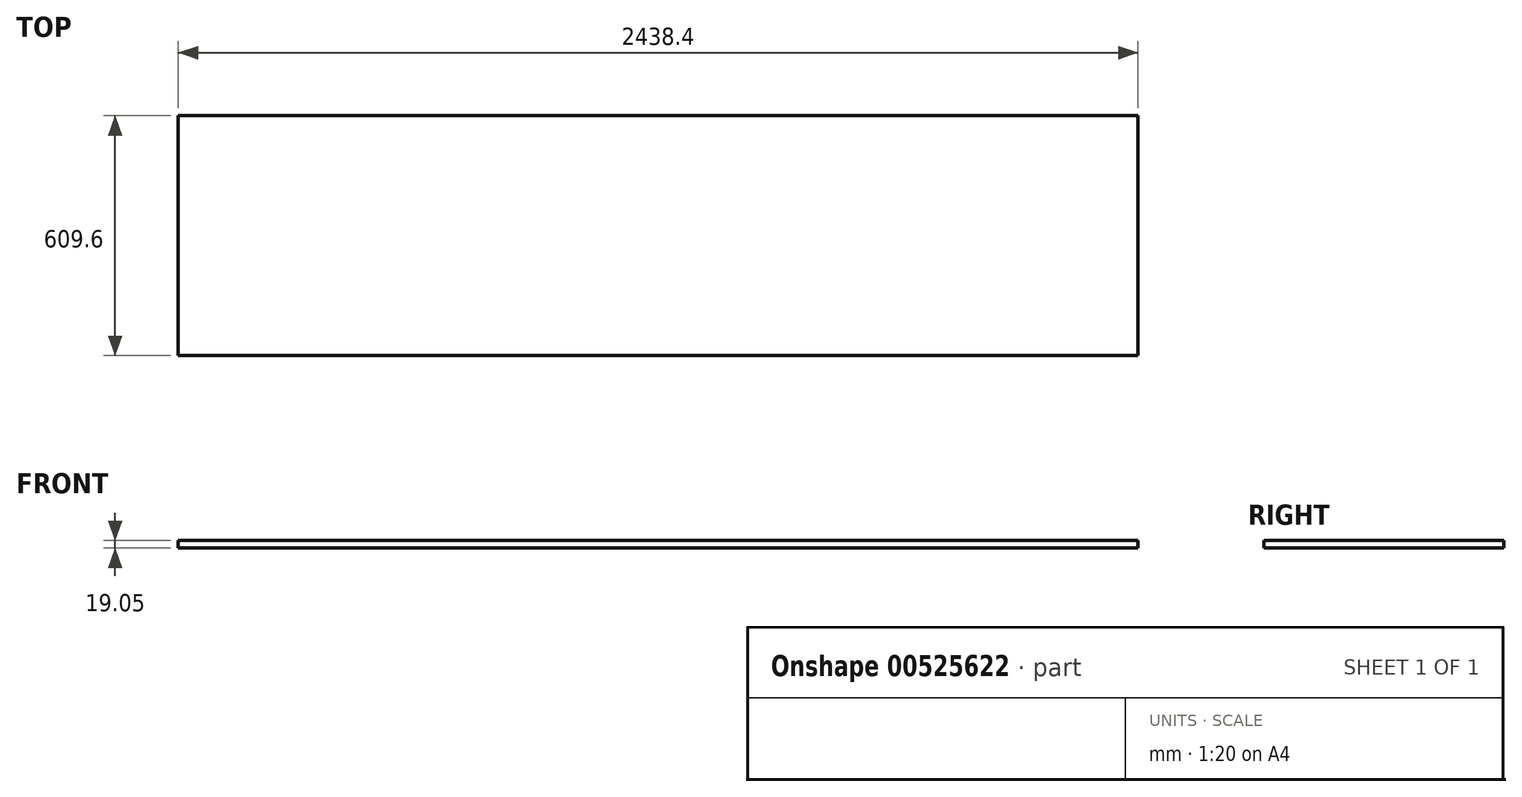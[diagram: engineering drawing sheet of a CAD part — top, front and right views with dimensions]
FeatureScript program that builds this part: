
annotation { "Feature Type Name" : "Feature", "Feature Type Description" : "" }
export const myFeature = defineFeature(function(context is Context, id is Id, definition is map)
    precondition{}
    {
        {
            var Q0;
            Q0=qCreatedBy(makeId("Top.planeOp"),FACE);
            var sketch = newSketch(context, id + "F0", { "sketchPlane" : qUnion([Q0])});
            skLineSegment(sketch, "E0.bottom", {"start": v(1219.2, -304.8) * mm, "end": v(-1219.2, -304.8) * mm});
            skLineSegment(sketch, "E0.top", {"start": v(1219.2, 304.8) * mm, "end": v(-1219.2, 304.8) * mm});
            skLineSegment(sketch, "E0.left", {"start": v(1219.2, -304.8) * mm, "end": v(1219.2, 304.8) * mm});
            skLineSegment(sketch, "E0.right", {"start": v(-1219.2, -304.8) * mm, "end": v(-1219.2, 304.8) * mm});
            skPoint(sketch, "E0.middle", {"position": v(0, 0) * mm});
            skSolve(sketch);
        }
        {
            var Q0;
            Q0 = qSketchRegion(id + "F0", true);
            extrude(context, id + "F1", {"entities" : qUnion([Q0]), "depth" : 19.05 * mm, "offsetDistance" : 25.4 * mm});
        }
    });
